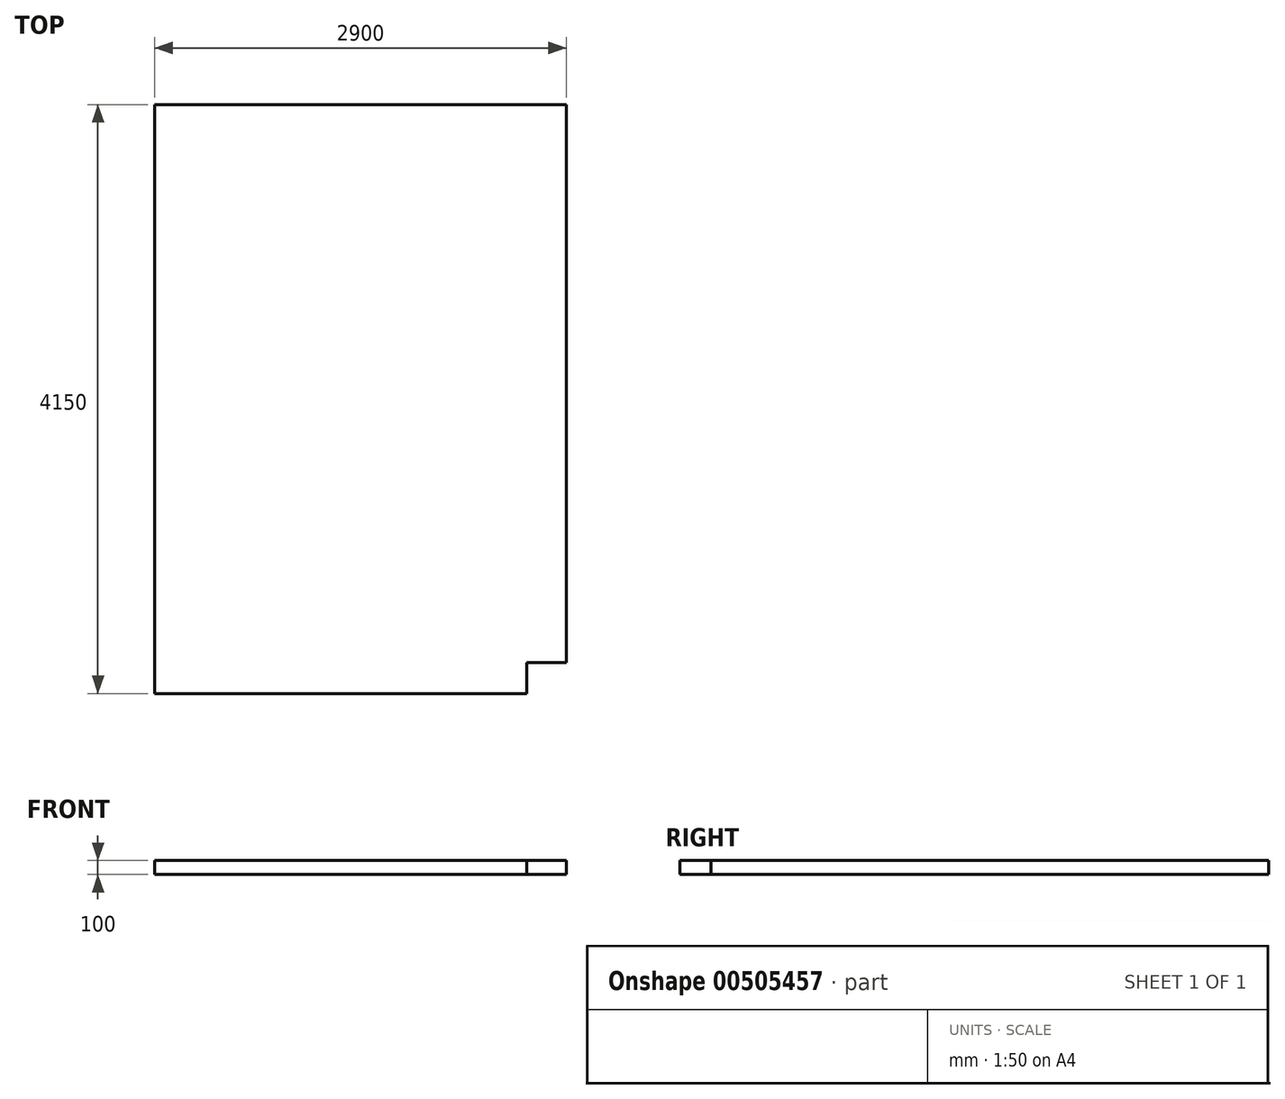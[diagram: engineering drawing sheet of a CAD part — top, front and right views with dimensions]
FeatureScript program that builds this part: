
annotation { "Feature Type Name" : "Feature", "Feature Type Description" : "" }
export const myFeature = defineFeature(function(context is Context, id is Id, definition is map)
    precondition{}
    {
        {
            var Q0;
            Q0=qCreatedBy(makeId("Top.planeOp"),FACE);
            var sketch = newSketch(context, id + "F0", { "sketchPlane" : qUnion([Q0])});
            skLineSegment(sketch, "E0.bottom", {"start": v(-1450, 2075) * mm, "end": v(1450, 2075) * mm});
            skLineSegment(sketch, "E0.top", {"start": v(-1450, -2075) * mm, "end": v(1170, -2075) * mm});
            skLineSegment(sketch, "E0.left", {"start": v(-1450, 2075) * mm, "end": v(-1450, -2075) * mm});
            skLineSegment(sketch, "E0.right", {"start": v(1450, 2075) * mm, "end": v(1450, -1855) * mm});
            skPoint(sketch, "E0.middle", {"position": v(0, 0) * mm});
            skLineSegment(sketch, "E1.top", {"start": v(1450, -1855) * mm, "end": v(1170, -1855) * mm});
            skLineSegment(sketch, "E1.right", {"start": v(1170, -2075) * mm, "end": v(1170, -1855) * mm});
            skSolve(sketch);
        }
        {
            var Q0;
            Q0 = qSketchRegion(id + "F0", true);
            extrude(context, id + "F1", {"entities" : qUnion([Q0]), "depth" : 100 * mm});
        }
    });
